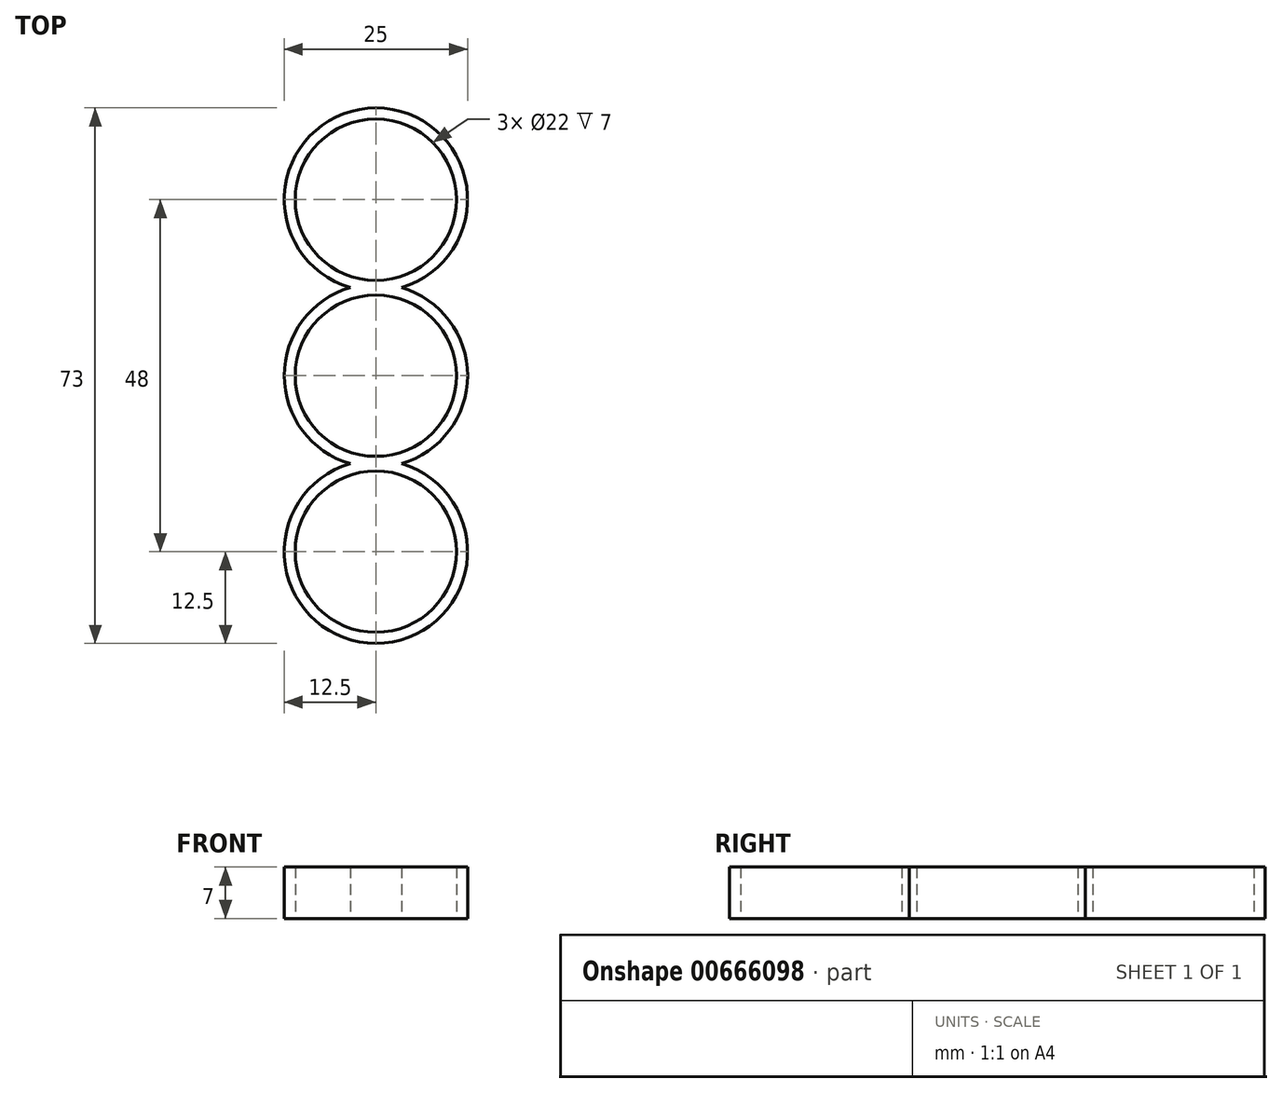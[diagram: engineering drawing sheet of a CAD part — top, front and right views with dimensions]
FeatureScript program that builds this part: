
annotation { "Feature Type Name" : "Feature", "Feature Type Description" : "" }
export const myFeature = defineFeature(function(context is Context, id is Id, definition is map)
    precondition{}
    {
        {
            var Q0;
            Q0=qCreatedBy(makeId("Top.planeOp"),FACE);
            var sketch = newSketch(context, id + "F0", { "sketchPlane" : qUnion([Q0])});
            skArc(sketch, "E0", {"start": v(11, 0) * mm, "mid": v(0, 11) * mm, "end": v(-11, 0) * mm});
            skArc(sketch, "E1", {"start": v(-3.5, 12) * mm, "mid": v(-10, 7.5) * mm, "end": v(-12.5, 0) * mm});
            skCircle(sketch, "E2", {"center": v(0, 24) * mm, "radius": 11 * mm});
            skArc(sketch, "E3", {"start": v(3.5, 12) * mm, "mid": v(0, 36.5) * mm, "end": v(-3.5, 12) * mm});
            skArc(sketch, "E4.trimOffspring", {"start": v(12.5, 0) * mm, "mid": v(10, 7.5) * mm, "end": v(3.5, 12) * mm});
            skCircle(sketch, "E5.MirrorC", {"center": v(0, -24) * mm, "radius": 11 * mm});
            skArc(sketch, "E6.MirrorCS", {"start": v(3.5, -12) * mm, "mid": v(0, -36.5) * mm, "end": v(-3.5, -12) * mm});
            skArc(sketch, "E7.MirrorCS", {"start": v(-3.5, -12) * mm, "mid": v(-10, -7.5) * mm, "end": v(-12.5, 0) * mm});
            skArc(sketch, "E8.MirrorCS", {"start": v(12.5, 0) * mm, "mid": v(10, -7.5) * mm, "end": v(3.5, -12) * mm});
            skArc(sketch, "E9.MirrorCS", {"start": v(11, 0) * mm, "mid": v(0, -11) * mm, "end": v(-11, 0) * mm});
            skSolve(sketch);
        }
        {
            var Q0;
            Q0 = qSketchRegion(id + "F0", true);
            extrude(context, id + "F1", {"entities" : qUnion([Q0]), "depth" : 7 * mm, "offsetDistance" : 25 * mm});
        }
    });
